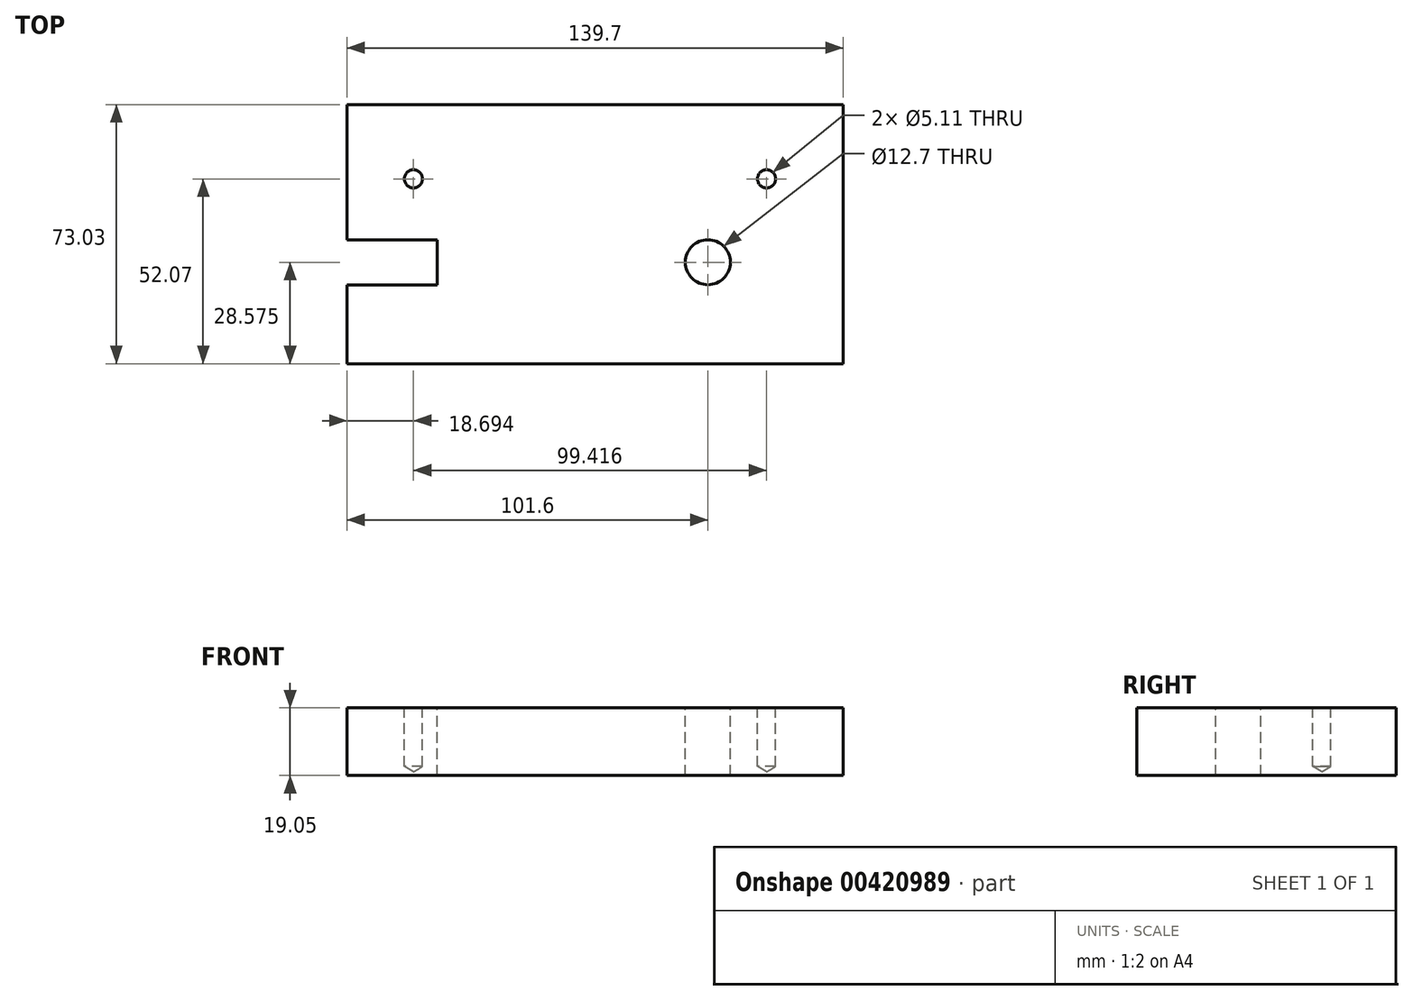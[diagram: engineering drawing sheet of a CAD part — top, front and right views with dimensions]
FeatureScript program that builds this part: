
annotation { "Feature Type Name" : "Feature", "Feature Type Description" : "" }
export const myFeature = defineFeature(function(context is Context, id is Id, definition is map)
    precondition{}
    {
        {
            var Q0;
            Q0=qCreatedBy(makeId("Top.planeOp"),FACE);
            var sketch = newSketch(context, id + "F0", { "sketchPlane" : qUnion([Q0])});
            skLineSegment(sketch, "E0.bottom", {"start": v(0, 0) * mm, "end": v(139.7, 0) * mm});
            skLineSegment(sketch, "E0.top", {"start": v(0, 73.03) * mm, "end": v(139.7, 73.03) * mm});
            skLineSegment(sketch, "E0.left", {"start": v(0, 0) * mm, "end": v(0, 73.03) * mm});
            skLineSegment(sketch, "E0.right", {"start": v(139.7, 0) * mm, "end": v(139.7, 73.02) * mm});
            skSolve(sketch);
        }
        {
            var Q0;
            Q0 = qSketchRegion(id + "F0", true);
            extrude(context, id + "F1", {"entities" : qUnion([Q0]), "depth" : 19.05 * mm});
        }
        {
            var Q0;
            Q0=makeQuery(id+"F1.opExtrude","CAP_FACE",FACE,{"disambiguationData":[OSD([sQuery(id+"F0.wireOp",EDGE,"E0.bottom"),sQuery(id+"F0.wireOp",EDGE,"E0.top"),sQuery(id+"F0.wireOp",EDGE,"E0.left"),sQuery(id+"F0.wireOp",EDGE,"E0.right")])],"isStart":false});
            var sketch = newSketch(context, id + "F2", { "sketchPlane" : qUnion([Q0])});
            skLineSegment(sketch, "E1", {"start": v(139.7, 28.58) * mm, "end": v(101.6, 28.57) * mm, "construction": true});
            skLineSegment(sketch, "E2.bottom", {"start": v(0, 22.23) * mm, "end": v(25.4, 22.23) * mm});
            skLineSegment(sketch, "E2.top", {"start": v(0, 34.92) * mm, "end": v(25.4, 34.92) * mm});
            skLineSegment(sketch, "E2.left", {"start": v(0, 22.23) * mm, "end": v(0, 34.92) * mm});
            skLineSegment(sketch, "E2.right", {"start": v(25.4, 22.23) * mm, "end": v(25.4, 34.92) * mm});
            skCircle(sketch, "E3", {"center": v(101.6, 28.57) * mm, "radius": 6.35 * mm});
            skSolve(sketch);
        }
        {
            var Q0;
            Q0 = qSketchRegion(id + "F2", true);
            extrude(context, id + "F3", {"entities" : qUnion([Q0]), "operationType" : NewBodyOperationType.REMOVE, "oppositeDirection" : true, "depth" : 25.4 * mm});
        }
        {
            var Q0;
            Q0=makeQuery(id+"F1.opExtrude","CAP_FACE",FACE,{"disambiguationData":[OSD([sQuery(id+"F0.wireOp",EDGE,"E0.bottom"),sQuery(id+"F0.wireOp",EDGE,"E0.top"),sQuery(id+"F0.wireOp",EDGE,"E0.left"),sQuery(id+"F0.wireOp",EDGE,"E0.right")])],"isStart":false});
            var sketch = newSketch(context, id + "F4", { "sketchPlane" : qUnion([Q0])});
            skLineSegment(sketch, "E4", {"start": v(18.7, 52.07) * mm, "end": v(118.11, 52.07) * mm, "construction": true});
            skPoint(sketch, "E5", {"position": v(18.7, 52.07) * mm});
            skPoint(sketch, "E6", {"position": v(118.11, 52.07) * mm});
            skSolve(sketch);
        }
        {
            var Q0;
            Q0=sQuery(id+"F4.wireOp",VERTEX,"E5");
            var Q1;
            Q1=sQuery(id+"F4.wireOp",VERTEX,"E6");
            var Q2;
            Q2=makeQuery(id+"F1.opExtrude","SWEPT_BODY",BODY,{"disambiguationData":[OSD([sQuery(id+"F0.wireOp",EDGE,"E0.bottom"),sQuery(id+"F0.wireOp",EDGE,"E0.top"),sQuery(id+"F0.wireOp",EDGE,"E0.left"),sQuery(id+"F0.wireOp",EDGE,"E0.right")])]});
            hole(context, id + "F5", {"style" : HoleStyle.SIMPLE, "endStyle" : HoleEndStyle.BLIND, "standardTappedOrClearance" : lookupTablePath({ "standard" : "ANSI", "engagement" : "75%", "pitch" : "20 tpi", "size" : "1/4", "type" : "Tapped" }), "standardBlindInLast" : lookupTablePath({ "standard" : "ANSI", "engagement" : "75%", "pitch" : "20 tpi", "size" : "1/4", "type" : "Tapped" }), "holeDiameter" : 5.1 * mm, "showTappedDepth" : true, "holeDepth" : 16.51 * mm, "isTappedThrough" : true, "tappedDepth" : 12.7 * mm, "tapClearance" : 3, "locations" : qUnion([Q0, Q1]), "scope" : qUnion([Q2]), "majorDiameter" : 6.35 * mm});
        }
    });
